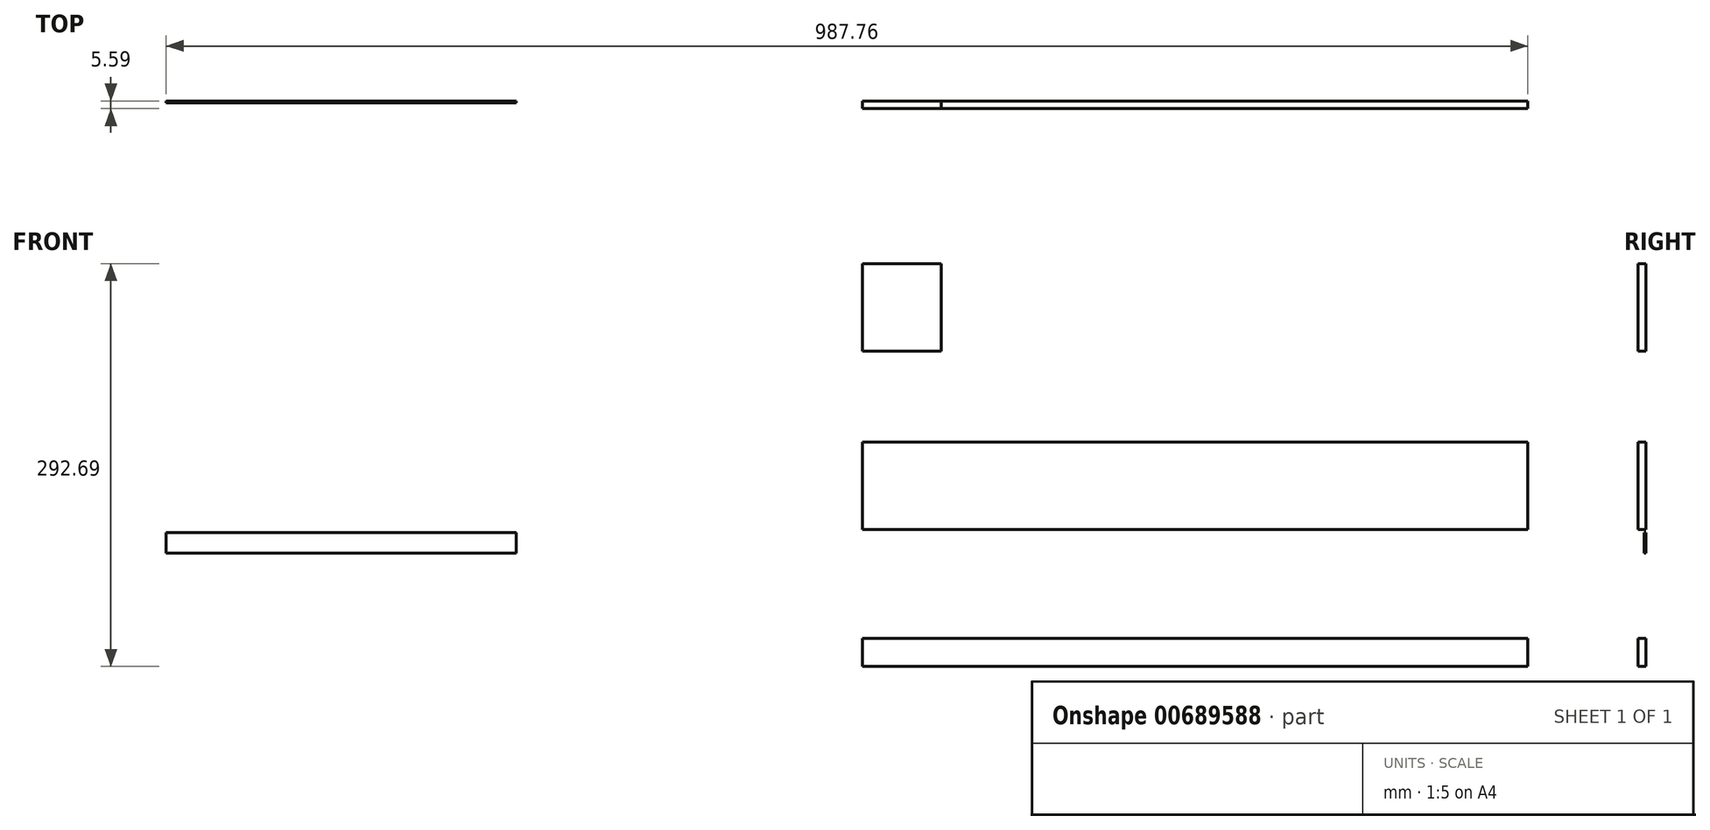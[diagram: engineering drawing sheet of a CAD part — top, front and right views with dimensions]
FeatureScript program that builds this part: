
annotation { "Feature Type Name" : "Feature", "Feature Type Description" : "" }
export const myFeature = defineFeature(function(context is Context, id is Id, definition is map)
    precondition{}
    {
        {
            var Q0;
            Q0=qCreatedBy(makeId("Front.planeOp"),FACE);
            var sketch = newSketch(context, id + "F0", { "sketchPlane" : qUnion([Q0])});
            skLineSegment(sketch, "E0.bottom", {"start": v(0, 0) * mm, "end": v(57.15, 0) * mm});
            skLineSegment(sketch, "E0.top", {"start": v(0, 63.5) * mm, "end": v(57.15, 63.5) * mm});
            skLineSegment(sketch, "E0.left", {"start": v(0, 0) * mm, "end": v(0, 63.5) * mm});
            skLineSegment(sketch, "E0.right", {"start": v(57.15, 0) * mm, "end": v(57.15, 63.5) * mm});
            skLineSegment(sketch, "E1.bottom", {"start": v(0, -66.21) * mm, "end": v(482.6, -66.21) * mm});
            skLineSegment(sketch, "E1.top", {"start": v(0, -129.71) * mm, "end": v(482.6, -129.71) * mm});
            skLineSegment(sketch, "E1.left", {"start": v(0, -66.21) * mm, "end": v(0, -129.71) * mm});
            skLineSegment(sketch, "E1.right", {"start": v(482.6, -66.21) * mm, "end": v(482.6, -129.71) * mm});
            skLineSegment(sketch, "E2.bottom", {"start": v(0, -208.87) * mm, "end": v(482.6, -208.87) * mm});
            skLineSegment(sketch, "E2.top", {"start": v(0, -229.19) * mm, "end": v(482.6, -229.19) * mm});
            skLineSegment(sketch, "E2.left", {"start": v(0, -208.87) * mm, "end": v(0, -229.19) * mm});
            skLineSegment(sketch, "E2.right", {"start": v(482.6, -208.87) * mm, "end": v(482.6, -229.19) * mm});
            skSolve(sketch);
        }
        {
            var Q0;
            Q0=makeQuery(id+"F0.imprint","IMPRINT",FACE,{"disambiguationData":[TD([[makeQuery(id+"F0.imprint","IMPRINT",EDGE,{"derivedFrom":sQuery(id+"F0.wireOp",EDGE,"E0.bottom")}),1.0]])]});
            var Q1;
            Q1=makeQuery(id+"F0.imprint","IMPRINT",FACE,{"disambiguationData":[TD([[makeQuery(id+"F0.imprint","IMPRINT",EDGE,{"derivedFrom":sQuery(id+"F0.wireOp",EDGE,"E1.bottom")}),-1.0]])]});
            var Q2;
            Q2=makeQuery(id+"F0.imprint","IMPRINT",FACE,{"disambiguationData":[TD([[makeQuery(id+"F0.imprint","IMPRINT",EDGE,{"derivedFrom":sQuery(id+"F0.wireOp",EDGE,"goXvJbon-gzJT-NYTh-aRHv-xLW4f2k4YAFC.bottom")}),-1.0]])]});
            var Q3;
            Q3=makeQuery(id+"F0.imprint","IMPRINT",FACE,{"disambiguationData":[TD([[makeQuery(id+"F0.imprint","IMPRINT",EDGE,{"derivedFrom":sQuery(id+"F0.wireOp",EDGE,"E2.bottom")}),-1.0]])]});
            extrude(context, id + "F1", {"entities" : qUnion([Q0, Q1, Q2, Q3]), "depth" : 5.6 * mm, "offsetDistance" : 25 * mm});
        }
        {
            var Q0;
            Q0=qCreatedBy(makeId("Front.planeOp"),FACE);
            var sketch = newSketch(context, id + "F2", { "sketchPlane" : qUnion([Q0])});
            skLineSegment(sketch, "E3.bottom", {"start": v(-505.16, -131.8) * mm, "end": v(-251.16, -131.8) * mm});
            skLineSegment(sketch, "E3.top", {"start": v(-505.16, -146.8) * mm, "end": v(-251.16, -146.8) * mm});
            skLineSegment(sketch, "E3.left", {"start": v(-505.16, -131.8) * mm, "end": v(-505.16, -146.8) * mm});
            skLineSegment(sketch, "E3.right", {"start": v(-251.16, -131.8) * mm, "end": v(-251.16, -146.8) * mm});
            skSolve(sketch);
        }
        {
            var Q0;
            Q0=makeQuery(id+"F2.imprint","IMPRINT",FACE,{"disambiguationData":[TD([[makeQuery(id+"F2.imprint","IMPRINT",EDGE,{"derivedFrom":sQuery(id+"F2.wireOp",EDGE,"E3.bottom")}),-1.0]])]});
            extrude(context, id + "F3", {"entities" : qUnion([Q0]), "depth" : 1.27 * mm, "offsetDistance" : 25 * mm});
        }
    });
